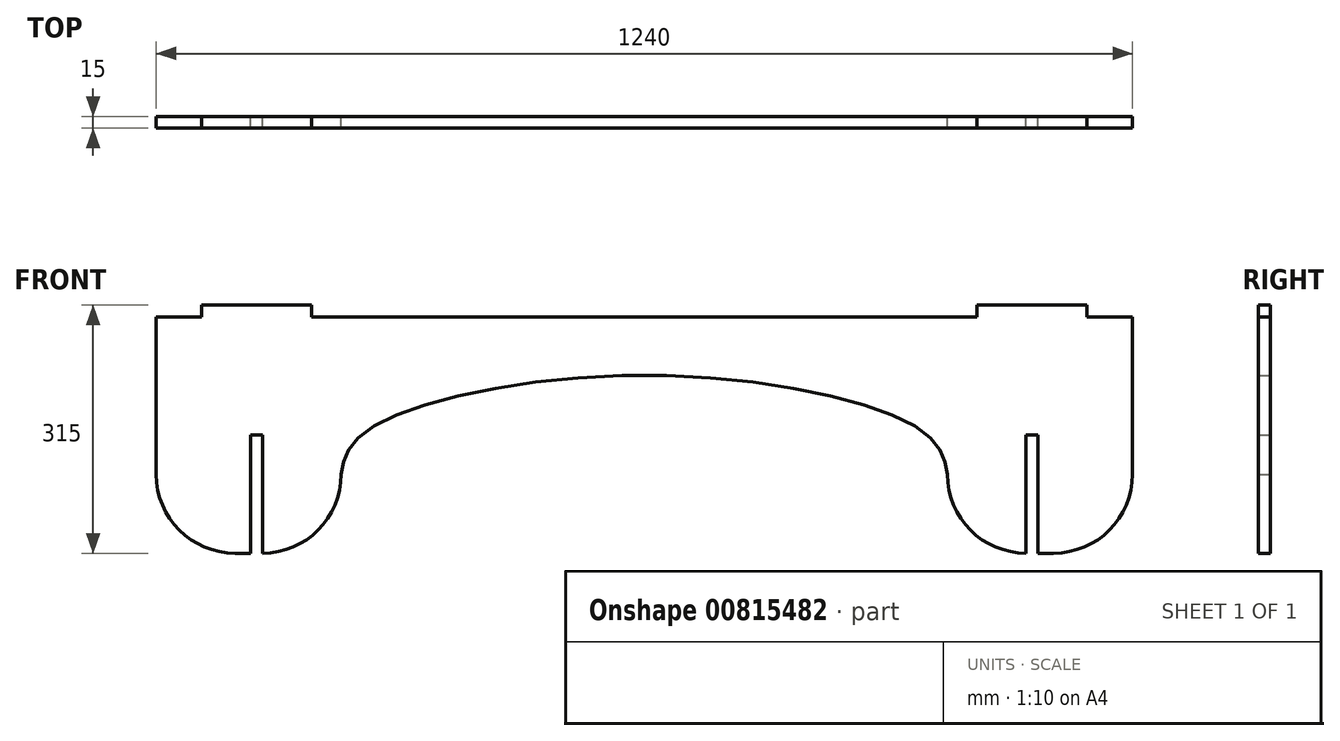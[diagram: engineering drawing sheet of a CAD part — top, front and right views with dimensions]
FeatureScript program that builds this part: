
annotation { "Feature Type Name" : "Feature", "Feature Type Description" : "" }
export const myFeature = defineFeature(function(context is Context, id is Id, definition is map)
    precondition{}
    {
        {
            var Q0;
            Q0=qCreatedBy(makeId("Front.planeOp"),FACE);
            var sketch = newSketch(context, id + "F0", { "sketchPlane" : qUnion([Q0])});
            skLineSegment(sketch, "E0.bottom", {"start": v(-620, 150) * mm, "end": v(-562.5, 150) * mm});
            skLineSegment(sketch, "E0.top", {"start": v(-520, -150) * mm, "end": v(-500, -150) * mm});
            skLineSegment(sketch, "E0.left", {"start": v(-620, 150) * mm, "end": v(-620, -50) * mm});
            skLineSegment(sketch, "E0.right", {"start": v(620, 150) * mm, "end": v(620, -50) * mm});
            skLineSegment(sketch, "E1.top", {"start": v(-500, 0) * mm, "end": v(-485, 0) * mm});
            skLineSegment(sketch, "E2", {"start": v(-500, 0) * mm, "end": v(-500, -150) * mm});
            skLineSegment(sketch, "E3", {"start": v(-485, 0) * mm, "end": v(-485, -150) * mm});
            skLineSegment(sketch, "E4.trimOffspring", {"start": v(-485, -150) * mm, "end": v(-485, -150) * mm});
            skLineSegment(sketch, "E5.bottom", {"start": v(485, 0) * mm, "end": v(500, 0) * mm});
            skLineSegment(sketch, "E6", {"start": v(485, 0) * mm, "end": v(485, -150) * mm});
            skLineSegment(sketch, "E7", {"start": v(500, 0) * mm, "end": v(500, -150) * mm});
            skLineSegment(sketch, "E8.trimOffspring", {"start": v(500, -150) * mm, "end": v(520, -150) * mm});
            skPoint(sketch, "E9.visualSharp", {"position": v(-620, -150) * mm});
            skArc(sketch, "E9.filletArc", {"start": v(-620, -50) * mm, "mid": v(-590.71, -120.71) * mm, "end": v(-520, -150) * mm});
            skPoint(sketch, "E10.visualSharp", {"position": v(620, -150) * mm});
            skArc(sketch, "E10.filletArc", {"start": v(520, -150) * mm, "mid": v(590.71, -120.71) * mm, "end": v(620, -50) * mm});
            skLineSegment(sketch, "E11", {"start": v(-385, -50) * mm, "end": v(-385, -50) * mm});
            skPoint(sketch, "E12.newPointB", {"position": v(-385, -150) * mm});
            skArc(sketch, "E12.filletArc", {"start": v(-485, -150) * mm, "mid": v(-414.29, -120.71) * mm, "end": v(-385, -50) * mm});
            skLineSegment(sketch, "E13", {"start": v(485, -150) * mm, "end": v(485, -150) * mm});
            skPoint(sketch, "E14.visualSharp", {"position": v(385, -150) * mm});
            skArc(sketch, "E14.filletArc", {"start": v(385, -50) * mm, "mid": v(414.29, -120.71) * mm, "end": v(485, -150) * mm});
            skLineSegment(sketch, "E15", {"start": v(385, -50) * mm, "end": v(385, -50) * mm});
            skPoint(sketch, "E16.visualSharp", {"position": v(-385, -25) * mm});
            skPoint(sketch, "E17.visualSharp", {"position": v(385, -25) * mm});
            skLineSegment(sketch, "E18.right", {"start": v(-562.5, 150) * mm, "end": v(-562.5, 165) * mm});
            skLineSegment(sketch, "E19.right", {"start": v(-422.5, 150) * mm, "end": v(-422.5, 165) * mm});
            skLineSegment(sketch, "E20", {"start": v(-562.5, 165) * mm, "end": v(-422.5, 165) * mm});
            skLineSegment(sketch, "E21.trimOffspring", {"start": v(-422.5, 150) * mm, "end": v(422.5, 150) * mm});
            skPoint(sketch, "E22.orphan", {"position": v(-500, 150) * mm});
            skPoint(sketch, "E19.bottom.start.orphan", {"position": v(-485, 150) * mm});
            skLineSegment(sketch, "E23.right", {"start": v(562.5, 150) * mm, "end": v(562.5, 165) * mm});
            skLineSegment(sketch, "E24.right", {"start": v(422.5, 150) * mm, "end": v(422.5, 165) * mm});
            skLineSegment(sketch, "E25", {"start": v(422.5, 165) * mm, "end": v(562.5, 165) * mm});
            skLineSegment(sketch, "E26.trimOffspring", {"start": v(562.5, 150) * mm, "end": v(620, 150) * mm});
            skPoint(sketch, "E24.bottom.start.orphan", {"position": v(485, 150) * mm});
            skPoint(sketch, "E23.bottom.start.orphan", {"position": v(500, 150) * mm});
            skFitSpline(sketch, "E27", {"points": [v(-385, -50) * mm, v(-360, 0) * mm, v(0, 76.04) * mm, v(360, 0) * mm, v(385, -50) * mm], "startDerivative": vector(62.96, 363.3) * mm, "endDerivative": vector(62.96, -363.3) * mm});
            skPoint(sketch, "E28.orphan", {"position": v(-360, -25) * mm});
            skPoint(sketch, "E29.orphan", {"position": v(360, -25) * mm});
            skSolve(sketch);
        }
        {
            var Q0;
            Q0=makeQuery(id+"F0.imprint","IMPRINT",FACE,{"disambiguationData":[TD([[makeQuery(id+"F0.imprint","IMPRINT",EDGE,{"derivedFrom":sQuery(id+"F0.wireOp",EDGE,"E0.bottom")}),-1.0]])]});
            extrude(context, id + "F1", {"entities" : qUnion([Q0]), "depth" : 15 * mm, "offsetDistance" : 25 * mm});
        }
    });
